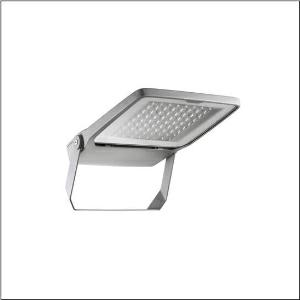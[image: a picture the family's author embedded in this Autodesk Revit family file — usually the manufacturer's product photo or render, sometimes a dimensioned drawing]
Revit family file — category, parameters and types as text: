
# Revit family: floodlight_fl_20_mini___pl61_5xa7672b1c1ac_e27e
name_source: partatom
category: Lighting Fixtures
units: mm (PartAtom-declared; Revit-internal decimal feet)

## family parameters
Cut with Voids When Loaded = No
Host = Face
Light Source = No
Part Type = Normal
Room Calculation Point = No
Round Connector Dimension = Use Diameter
Shared = No

## types (1)
- --- (1 x LED 3000K / CRI = 80 (unbekannt), 4980 lm, 3000K)
    Apparent Load = 51 VA
    CIE Flux Codes = 33 65 98 100 100
    Color Rendering = 80
    Color Temperature = 3000K
    Default Elevation = 1800 mm
    Description = Floodlight FL 20 mini, floodlight, primary light control with lens, of plastic, primary optical cover: protective disc, of toughened safety glass, transparent, light distribution: PL61, light emission: direct distribution, primary light characteristic: asymmetric, installation type: surface-mounted, LED, High Power LED, rated luminous flux: 4.980lm, luminous efficacy: 98lm/W, light colour: 830, colour temperature: 3000K, control gear: ECG Plus, control: flexible luminous flux parameterisation, time-dependent luminous flux control, digital communication interface, power reduction, overheat protection, electronic power reduction, with terminal, 5-pole, max. 2.5mm², mains connection: 220..240V, AC, 50/60Hz, rated input power: 51W, LED unit, of diecast aluminium, powder-coated, Siteco® metallic grey (DB 702S), corrosivity category C5 mid according to DIN EN ISO 12944, incl. 1x M20 cable gland for cable Ø 6.5..12mm, length: 446mm, width: 355mm, height: 62mm, housing frame, of diecast aluminium, powder-coated, Siteco® metallic grey (DB 702S), mounting bracket, of steel, powder-coated, Siteco® metallic grey (DB 702S), DALI, protection rating (complete): IP66, insulation class (complete): insulation class II (safety insulation), certification: CE, ENEC, VDE, protection symbol: D, permissible operating ambient temperature: -40..+40°C, permissible operating ambient temperature for outdoor applications: -40..+50°C, standard: DIN EN 12944, packaging unit: 1 piece

Light Distribution: PL61
    Height = 62 mm  [stored 0.203412 ft]
    Lamp = 1 x LED 3000K / CRI >= 80 (unbekannt)
    Lamp Light Flux = 4980 lm
    Lamp count = 1
    Length = 467 mm
    Luminous efficacy = 98 lm/W
    Manufacturer = Siteco
    ModVariant = No
    Model = 5XA7672B1C1AC
    Mounting Place = Wall
    Mounting Type = Surface mounted
    Number of Poles = 1
    OnlyDefault = Yes
    Power Factor = 1
    Product Name = Floodlight FL 20 mini | PL61
    Product group = floodlight | wall mounted
    ProductGroupID = 2001
    Protection Class = Protection class II
    Protection Degree = IP 66
    RLX_Detail_Level = 1
    RLX_Emergency_Light_Flux = 0 lm
    RLX_Emergency_Type = 0
    RLX_Emergency_Type_DB = No
    RlxData = <blob elided: 74001 chars, md5=28c8b090>
    Socket = socket
    Standby Power = 0 W
    System Light Flux = 4980 lm
    System Power = 51 W
    Type Comments = factory setting: luminous flux: 100 % | dim-lin: 254 | 520 mA
    Type Image = l_1005948.jpg
    URL = http://relux.com
    VarID = @adj_163557
    Voltage = 0 V
    Weight = 0.00 kg
    Width = 335 mm

note: [stored X ft] marks values corroborated as IEEE doubles in the binary element streams (Revit-internal decimal feet)

## geometry (parser evidence)
native form markers: Blend x4, Sweep x12
no freeform markers — native parametric forms only
